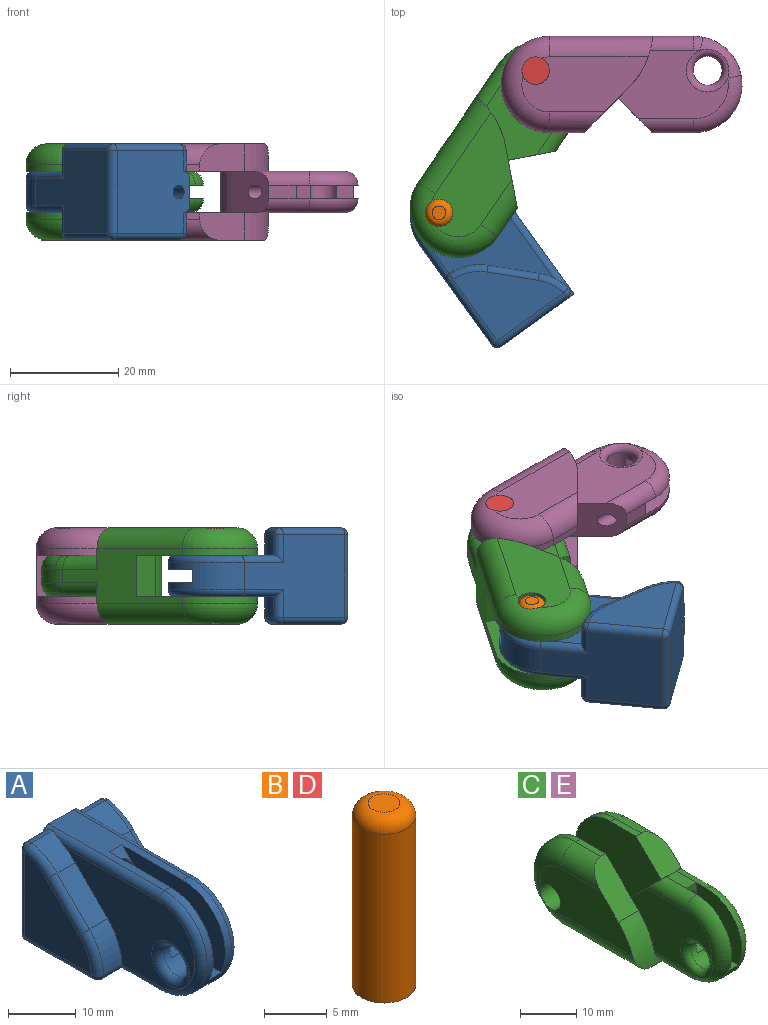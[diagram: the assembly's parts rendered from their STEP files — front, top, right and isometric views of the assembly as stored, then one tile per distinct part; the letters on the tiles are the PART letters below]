
ASSEMBLY  parts=5 mates=8
PART A: 52 faces, bbox 17.8x33.8x19.2 mm
  f0: plane 7.62x7.62mm, normal (0,-0.71,0.71), area 23.8mm2, adj f10,f11,f14,f16
  f1: plane 24.13x5.08mm, normal (0,0,1), area 90.3mm2, adj f3,f7,f10,f11,f15,f23,f26
  f2: cylinder r=2.67mm len=5.33mm, axis (1,0,0), area 57.1mm2, adj f10,f11,f12,f13,f50,f51
  f3: cylinder r=8.89mm len=17.78mm, axis (-1,0,0), area 96.4mm2, adj f1,f9,f10,f11,f12,f24,f27
  f4: plane 27.22x15.24mm, normal (-1,0,0), area 226.5mm2, adj f18,f19,f22,f23,f24,f25,f49,f50
  f5: plane 27.22x15.24mm, normal (1,0,0), area 226.5mm2, adj f17,f20,f21,f26,f27,f28,f42,f51
  f6: plane 15.09x13.96mm, normal (1,0,0), area 138.1mm2, adj f33,f35,f38,f39,f40
  f7: plane 16.51x15.24mm, normal (0,1,0), area 235mm2, adj f1,f16,f23,f26,f29,f32,f35,f36
  f8: plane 15.09x13.96mm, normal (-1,0,0), area 138.1mm2, adj f29,f30,f45,f46,f47
  f9: plane 22.86x15.24mm, normal (0,0,-1), area 258mm2, adj f3,f25,f28,f30,f32,f33,f42,f49
  f10: plane 21.59x12.7mm, normal (-1,0,0), area 161.1mm2, adj f0,f1,f2,f3,f12,f13,f14,f15
  f11: plane 21.59x12.7mm, normal (1,0,0), area 161.1mm2, adj f0,f1,f2,f3,f12,f13,f14,f15
  f12: plane 3.15x2.54mm, normal (0,0,1), area 8mm2, adj f2,f3,f10,f11
  f13: plane 2.73x2.54mm, normal (0,0,1), area 6.9mm2, adj f2,f10,f11,f14
  f14: plane 2.54x2.54mm, normal (0,-1,0), area 6.5mm2, adj f0,f10,f11,f13
  f15: plane 2.54x2.54mm, normal (0,-0.71,0.71), area 5.5mm2, adj f1,f10,f11,f16
  f16: cylinder r=1.27mm len=15.24mm, axis (0,1,0), area 111.5mm2, adj f0,f7,f15
  f17: plane 6.76x6.76mm, normal (0,-0.71,0.71), area 36.4mm2, adj f5,f20,f21,f39
  f18: plane 6.76x6.76mm, normal (0,-0.71,0.71), area 36.4mm2, adj f4,f19,f22,f46
  f19: cylinder r=10.16mm len=6.73mm, axis (1,0,0), area 28.7mm2, adj f4,f18,f47,f49
  f20: cylinder r=10.16mm len=6.73mm, axis (1,0,0), area 28.7mm2, adj f5,f17,f40,f42
  f21: cylinder r=10.16mm len=5.27mm, axis (-1,0,0), area 23.8mm2, adj f5,f17,f26,f36,f38
  f22: cylinder r=10.16mm len=5.27mm, axis (-1,0,0), area 23.8mm2, adj f4,f18,f23,f43,f45
  f23: cylinder r=1.27mm len=24.13mm, axis (0,1,0), area 44.5mm2, adj f1,f4,f7,f22,f24,f43
  f24: torus R=7.62mm, axis (1,0,0), area 52.8mm2, adj f3,f4,f23,f25
  f25: cylinder r=1.27mm len=8.9mm, axis (0,-1,0), area 16.1mm2, adj f4,f9,f24,f49
  f26: cylinder r=1.27mm len=24.13mm, axis (0,-1,0), area 44.5mm2, adj f1,f5,f7,f21,f27,f36
  f27: torus R=7.62mm, axis (1,0,0), area 52.8mm2, adj f3,f5,f26,f28
  f28: cylinder r=1.27mm len=8.9mm, axis (0,1,0), area 16.1mm2, adj f5,f9,f27,f42
  f29: cylinder r=1.27mm len=15.09mm, axis (0,0,-1), area 30.1mm2, adj f7,f8,f31,f44
  f30: cylinder r=1.27mm len=13.96mm, axis (0,-1,0), area 27.9mm2, adj f8,f9,f31,f48
  f31: sphere r=1.27mm, area 2.5mm2, adj f29,f30,f32
  f32: cylinder r=1.27mm len=15.24mm, axis (-1,0,0), area 30.4mm2, adj f7,f9,f31,f34
  f33: cylinder r=1.27mm len=13.96mm, axis (0,1,0), area 27.9mm2, adj f6,f9,f34,f41
  f34: sphere r=1.27mm, area 2.5mm2, adj f32,f33,f35
  f35: cylinder r=1.27mm len=15.09mm, axis (0,0,1), area 30.1mm2, adj f6,f7,f34,f37
  f36: cylinder r=1.27mm len=4.48mm, axis (-1,0,0), area 9.2mm2, adj f7,f21,f26,f37
  f37: sphere r=1.27mm, area 2.8mm2, adj f35,f36,f38
  f38: torus R=8.89mm, axis (-1,0,0), area 11.5mm2, adj f6,f21,f37,f39
  f39: cylinder r=1.27mm len=7.65mm, axis (0,0.71,0.71), area 19.1mm2, adj f6,f17,f38,f40
  f40: torus R=8.89mm, axis (-1,0,0), area 14.3mm2, adj f6,f20,f39,f41
  f41: sphere r=1.27mm, area 2.6mm2, adj f33,f40,f42
  f42: cylinder r=1.27mm len=5.08mm, axis (1,0,0), area 8.7mm2, adj f5,f9,f20,f28,f41
  f43: cylinder r=1.27mm len=4.48mm, axis (-1,0,0), area 9.2mm2, adj f7,f22,f23,f44
  f44: sphere r=1.27mm, area 2.8mm2, adj f29,f43,f45
  f45: torus R=8.89mm, axis (-1,0,0), area 11.5mm2, adj f8,f22,f44,f46
  f46: cylinder r=1.27mm len=7.65mm, axis (0,0.71,0.71), area 19.1mm2, adj f8,f18,f45,f47
  f47: torus R=8.89mm, axis (-1,0,0), area 14.3mm2, adj f8,f19,f46,f48
  f48: sphere r=1.27mm, area 2.6mm2, adj f30,f47,f49
  f49: cylinder r=1.27mm len=5.08mm, axis (1,0,0), area 8.7mm2, adj f4,f9,f19,f25,f48
  f50: torus R=3.94mm, axis (1,0,0), area 39.2mm2, adj f2,f4
  f51: torus R=3.94mm, axis (1,0,0), area 39.2mm2, adj f2,f5
PART B: 4 faces, bbox 5.5x5.5x17.8 mm
  f0: cylinder r=2.54mm len=16.51mm, axis (0,0,-1), area 263.5mm2, adj f2,f3
  f1: plane 2.54x2.54mm, normal (0,0,1), area 5.1mm2, adj f3
  f2: plane 5.08x5.08mm, normal (0,0,-1), area 20.3mm2, adj f0
  f3: torus R=1.27mm, axis (0,0,1), area 26.1mm2, adj f0,f1
PART C: 48 faces, bbox 18.8x47x20.3 mm
  f0: plane 8.29x8.29mm, normal (0,-0.71,0.71), area 55.2mm2, adj f2,f3,f12,f13,f27,f32
  f1: plane 21.59x17.78mm, normal (-1,0,0), area 284.6mm2, adj f4,f11,f14,f15,f18,f25,f28,f29
  f2: plane 20.32x12.7mm, normal (-1,0,0), area 159.1mm2, adj f0,f27,f28,f30,f38,f39,f41,f42
  f3: plane 6.35x1.27mm, normal (0,0,1), area 8.1mm2, adj f0,f12,f16,f32
  f4: plane 6.35x1.27mm, normal (0,0,1), area 8.1mm2, adj f1,f15,f25,f35
  f5: plane 5.08x2.54mm, normal (0,0,1), area 12.9mm2, adj f22,f28,f38,f47
  f6: cylinder r=2.67mm len=5.33mm, axis (1,0,0), area 57.1mm2, adj f19,f20,f21,f24,f30,f31
  f7: cylinder r=8.89mm len=8.03mm, axis (-1,0,0), area 25.5mm2, adj f14,f19,f40,f41,f44,f45
  f8: cylinder r=1.27mm len=8.89mm, axis (0,1,0), area 60.5mm2, adj f22,f23,f28
  f9: plane 20.32x12.7mm, normal (1,0,0), area 159.1mm2, adj f25,f26,f28,f31,f43,f44,f46,f47
  f10: plane 23.31x10.16mm, normal (1,0,0), area 174.6mm2, adj f18,f25,f26,f35,f36,f37
  f11: plane 7.62x6.26mm, normal (0,1,0), area 47.7mm2, adj f1,f12,f14,f29
  f12: plane 21.59x17.78mm, normal (1,0,0), area 284.6mm2, adj f0,f3,f11,f14,f16,f17,f28,f29
  f13: plane 23.31x10.16mm, normal (-1,0,0), area 174.6mm2, adj f0,f17,f27,f32,f33,f34
  f14: plane 26.67x10.16mm, normal (0,0,-1), area 135.5mm2, adj f1,f7,f11,f12,f15,f16,f26,f27
  f15: cylinder r=8.89mm len=17.78mm, axis (1,0,0), area 35.5mm2, adj f1,f4,f14,f36
  f16: cylinder r=8.89mm len=17.78mm, axis (1,0,0), area 35.5mm2, adj f3,f12,f14,f33
  f17: cylinder r=2.54mm len=5.08mm, axis (1,0,0), area 80.9mm2, adj f12,f13,f33
  f18: cylinder r=2.54mm len=5.08mm, axis (1,0,0), area 80.9mm2, adj f1,f10,f36
  f19: plane 3.15x2.54mm, normal (0,0,1), area 8mm2, adj f6,f7,f21,f24
  f20: plane 2.73x2.54mm, normal (0,0,1), area 6.9mm2, adj f6,f21,f23,f24
  f21: plane 12.82x11.55mm, normal (-1,0,0), area 109.5mm2, adj f6,f19,f20,f22,f23,f45,f46,f47
  f22: plane 2.54x2.54mm, normal (0,-1,0), area 3.9mm2, adj f5,f8,f21,f24
  f23: plane 10.16x2.54mm, normal (0,-1,0), area 23.3mm2, adj f8,f20,f21,f24
  f24: plane 12.93x11.65mm, normal (1,0,0), area 109.5mm2, adj f6,f19,f20,f22,f23,f38,f39,f40
  f25: plane 8.29x8.29mm, normal (0,-0.71,0.71), area 55.2mm2, adj f1,f4,f9,f10,f26,f35
  f26: cylinder r=15.24mm len=9.49mm, axis (1,0,0), area 52.5mm2, adj f9,f10,f14,f25,f37,f43
  f27: cylinder r=15.24mm len=9.49mm, axis (1,0,0), area 52.5mm2, adj f0,f2,f13,f14,f34,f42
  f28: plane 8.69x8.1mm, normal (0,0.71,0.71), area 64.7mm2, adj f1,f2,f5,f8,f9,f12,f29,f38
  f29: cylinder r=6.35mm len=7.62mm, axis (-1,0,0), area 38mm2, adj f1,f11,f12,f28
  f30: torus R=3.94mm, axis (1,0,0), area 39.2mm2, adj f2,f6,f40
  f31: torus R=3.94mm, axis (1,0,0), area 39.2mm2, adj f6,f9,f45
  f32: cylinder r=3.81mm len=10.16mm, axis (0,1,0), area 46.3mm2, adj f0,f3,f13,f33
  f33: torus R=5.08mm, axis (-1,0,0), area 137.3mm2, adj f13,f16,f17,f32,f34
  f34: cylinder r=3.81mm len=19.05mm, axis (0,-1,0), area 111.5mm2, adj f13,f14,f27,f33
  f35: cylinder r=3.81mm len=10.16mm, axis (0,-1,0), area 46.3mm2, adj f4,f10,f25,f36
  f36: torus R=5.08mm, axis (-1,0,0), area 137.3mm2, adj f10,f15,f18,f35,f37
  f37: cylinder r=3.81mm len=19.05mm, axis (0,1,0), area 111.5mm2, adj f10,f14,f26,f36
  f38: cylinder r=2.54mm len=10.16mm, axis (0,1,0), area 35.5mm2, adj f2,f5,f24,f28,f39
  f39: torus R=6.35mm, axis (1,0,0), area 55.9mm2, adj f2,f24,f38,f40
  f40: bspline ~7.54x7.54mm, area 31.5mm2, adj f7,f24,f30,f39,f41
  f41: torus R=6.35mm, axis (1,0,0), area 6mm2, adj f2,f7,f40,f42
  f42: cylinder r=2.54mm len=8.05mm, axis (0,-1,0), area 31.3mm2, adj f2,f14,f27,f41
  f43: cylinder r=2.54mm len=8.05mm, axis (0,1,0), area 31.3mm2, adj f9,f14,f26,f44
  f44: torus R=6.35mm, axis (1,0,0), area 6mm2, adj f7,f9,f43,f45
  f45: bspline ~7.54x7.54mm, area 31.9mm2, adj f7,f21,f31,f44,f46
  f46: torus R=6.35mm, axis (1,0,0), area 55.9mm2, adj f9,f21,f45,f47
  f47: cylinder r=2.54mm len=10.16mm, axis (0,-1,0), area 35.5mm2, adj f5,f9,f21,f28,f46
PART D: same geometry as B
PART E: same geometry as C
PLACE A rot(axis=(-0.69,-0.22,-0.69),154.9deg) t=(-48.79,-38.22,-11.43)mm
PLACE B rot(axis=(0,0,1),39.7deg) t=(-49.59,-26.27,-11.43)mm
PLACE C rot(axis=(0.69,-0.21,0.69),156deg) t=(-42.71,-4.84,-11.43)mm
PLACE D rot(axis=(0,-1,0),180deg) t=(-31.75,0,6.35)mm
PLACE E rot(axis=(0.58,-0.58,0.58),120deg) t=(-10.16,6.35,-11.43)mm
MATE cylindrical C.f30 <-> D.f0  axis (0,0,1) through (-31.75,0,-5.08)mm
MATE planar B.f0 <-> C.f10  axis (0,0,1) through (-49.59,-26.27,6.35)mm
MATE planar C.f9 <-> E.f1  axis (0,0,1) through (-32.71,-7.69,1.27)mm
MATE cylindrical A.f2 <-> B.f0  axis (0,0,1) through (-49.59,-26.27,-2.54)mm
MATE planar A.f5 <-> C.f1  axis (0,0,1) through (-42.04,-29.63,1.27)mm
MATE cylindrical D.f0 <-> E.f17  axis (0,0,1) through (-31.75,0,-1.9)mm
MATE planar D.f0 <-> E.f10  axis (0,0,1) through (-31.75,0,6.35)mm
MATE cylindrical B.f0 <-> C.f17  axis (0,0,-1) through (-49.59,-26.27,-3.17)mm
